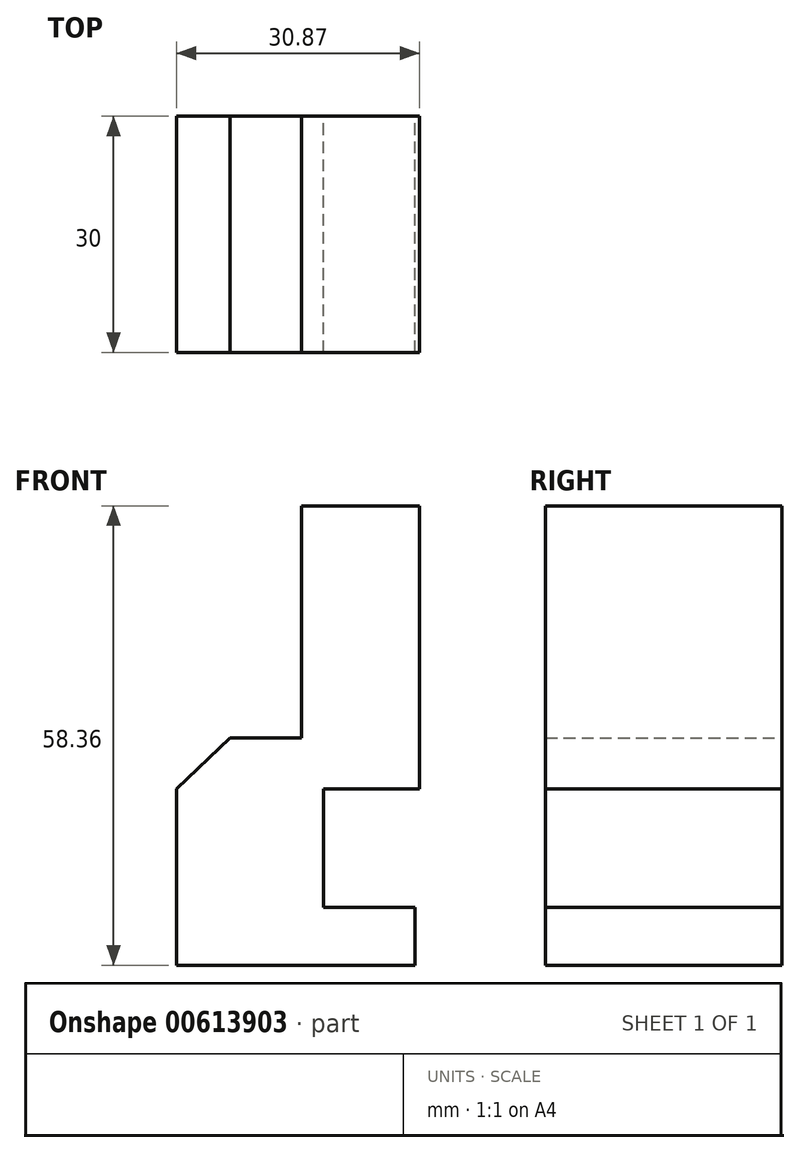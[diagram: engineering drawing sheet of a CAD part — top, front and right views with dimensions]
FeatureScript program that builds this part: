
annotation { "Feature Type Name" : "Feature", "Feature Type Description" : "" }
export const myFeature = defineFeature(function(context is Context, id is Id, definition is map)
    precondition{}
    {
        {
            var Q0;
            Q0=qCreatedBy(makeId("Front.planeOp"),FACE);
            var sketch = newSketch(context, id + "F0", { "sketchPlane" : qUnion([Q0])});
            skLineSegment(sketch, "E0", {"start": v(-24.22, 32.72) * mm, "end": v(-9.2, 32.72) * mm});
            skLineSegment(sketch, "E1", {"start": v(-9.2, 32.72) * mm, "end": v(-9.2, -3.26) * mm});
            skLineSegment(sketch, "E2", {"start": v(-9.2, -3.26) * mm, "end": v(-21.39, -3.26) * mm});
            skLineSegment(sketch, "E3", {"start": v(-21.39, -3.26) * mm, "end": v(-21.39, -18.27) * mm});
            skLineSegment(sketch, "E4", {"start": v(-21.39, -18.27) * mm, "end": v(-9.77, -18.27) * mm});
            skLineSegment(sketch, "E5", {"start": v(-9.77, -18.27) * mm, "end": v(-9.77, -25.64) * mm});
            skLineSegment(sketch, "E6", {"start": v(-9.77, -25.64) * mm, "end": v(-40.08, -25.64) * mm});
            skLineSegment(sketch, "E7", {"start": v(-40.08, -25.64) * mm, "end": v(-40.08, -3.26) * mm});
            skLineSegment(sketch, "E8", {"start": v(-40.08, -3.26) * mm, "end": v(-33.28, 3.26) * mm});
            skLineSegment(sketch, "E9", {"start": v(-33.28, 3.26) * mm, "end": v(-24.22, 3.26) * mm});
            skLineSegment(sketch, "E10", {"start": v(-24.22, 3.26) * mm, "end": v(-24.22, 32.72) * mm});
            skSolve(sketch);
        }
        {
            var Q0;
            Q0 = qSketchRegion(id + "F0", true);
            extrude(context, id + "F1", {"entities" : qUnion([Q0]), "depth" : 30 * mm, "offsetDistance" : 25 * mm});
        }
    });
